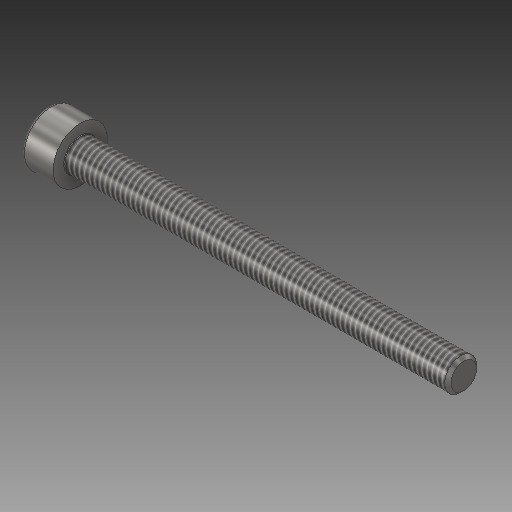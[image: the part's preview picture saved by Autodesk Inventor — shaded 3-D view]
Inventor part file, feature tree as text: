
AUTODESK INVENTOR PART (.ipt)
format: ipt  version: 2017 (Build 210142000, 142)  size: 195,072 bytes
history: native  units: mm
features: other x6, sketch x2, plane x1
ambient origin geometry x8: Origin, YZ Plane, XZ Plane, XY Plane, X Axis, Y Axis, Z Axis, Center Point
bodies: Solid1 (feature_tree)
feature tree (9):
  other  "ANSI B18.3.1M - M5x0.8 x 60NEW_MIR.ipt"
  other  "Solid1::ANSI B18.3.1M - M5x0.8 x 60NEW_MIR.ipt"
  other  "TaggingFeature1"
  sketch  "Sketch1"  dims[d0=10.0mm]
  sketch  "Sketch2"  dims[d19=0.0mm d28=0.0mm d29=0.0mm]
  plane  "Work Plane1"
  other  "Align 2D"
  other  "Align1"
  other  "Insert In1"
